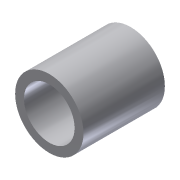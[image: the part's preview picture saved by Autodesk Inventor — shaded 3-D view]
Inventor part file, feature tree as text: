
AUTODESK INVENTOR PART (.ipt)
format: ipt  version: 2013 (Build 170138000, 138)  size: 81,920 bytes
history: native  units: in
note: dims shown in document units (in); Inventor stores cm internally (conversion verified against a paired STEP export)
features: extrude x1, sketch x1
ambient origin geometry x8: Origin, YZ Plane, XZ Plane, XY Plane, X Axis, Y Axis, Z Axis, Center Point
bodies: Solid1 (feature_tree)
feature tree (2):
  extrude  "Extrusion1"  Depth=0.84in
  sketch  "Sketch1"  dims[d0=0.622in d2=0.84in d3=1.0in d4=0.0in]
